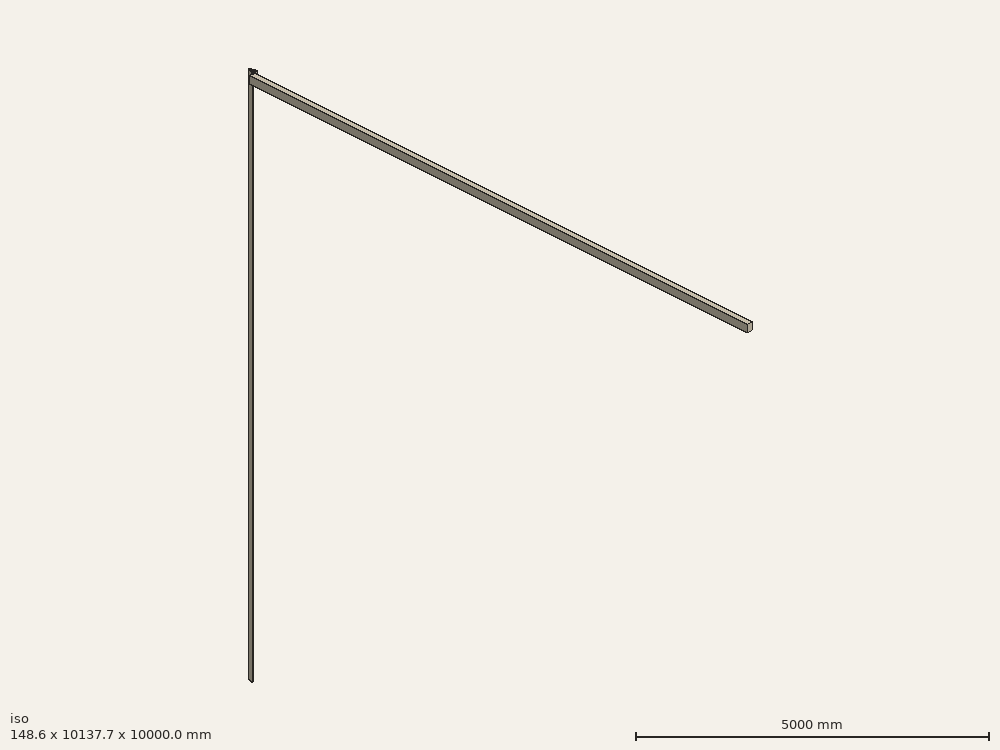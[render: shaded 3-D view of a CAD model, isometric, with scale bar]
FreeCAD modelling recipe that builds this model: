
FCSTD DOCUMENT  (FreeCAD 0.16R)
Label: iPadHolder
License: All rights reserved
LicenseURL: http://en.wikipedia.org/wiki/All_rights_reserved
objects: Sketcher::SketchObject×4, PartDesign::Chamfer×4, PartDesign::Pocket×3, PartDesign::Pad×1, Mesh::Feature×1
note: 16 computed .brp shape members not serialized (recipe doc carries the construction recipe); baked Part::Feature solids carry a one-line shape summary decoded from their .brp

FEATURE [Sketcher::SketchObject] Sketch
  sketch-geometry (27):
    g0: LineSegment StartX=-10 StartY=136.068 StartZ=0 EndX=-10 EndY=6.60009 EndZ=0
    g1: LineSegment StartX=-16.6001 StartY=0 StartZ=0 EndX=-78.7772 EndY=0 EndZ=0
    g2: LineSegment StartX=-80 StartY=-1.22284 StartZ=0 EndX=-80 EndY=-12.8107 EndZ=0
    g3: LineSegment StartX=-77.8107 StartY=-15 StartZ=0 EndX=25.8977 EndY=-15 EndZ=0
    g4: LineSegment StartX=28.76 StartY=-11.3687 StartZ=0 EndX=-6.74605 EndY=136.453 EndZ=0
    g5: LineSegment StartX=8.19725 StartY=15.8213 StartZ=0 EndX=15.8617 EndY=8.1568 EndZ=0
    g6: LineSegment StartX=15.8617 StartY=2.27255 StartZ=0 EndX=9.06464 EndY=-4.52454 EndZ=0
    g7: LineSegment StartX=7.32986 StartY=-4.52454 StartZ=0 EndX=-0.53498 EndY=3.3403 EndZ=0
    g8: LineSegment StartX=-0.53498 StartY=7.08905 StartZ=0 EndX=8.19725 EndY=15.8213 EndZ=0
    g9: LineSegment StartX=-2.82086 StartY=88.5548 StartZ=0 EndX=-4.52651 EndY=31.7136 EndZ=0
    g10: LineSegment StartX=-1.22545 StartY=28.2083 StartZ=0 EndX=8.07744 EndY=27.9291 EndZ=0
    g11: LineSegment StartX=11.5203 StartY=31.9185 StartZ=0 EndX=2.8702 EndY=80.3321 EndZ=0
    g12: LineSegment StartX=2.8702 StartY=80.3321 StartZ=0 EndX=-2.82086 EndY=88.5548 EndZ=0
    g13: ArcOfCircle CenterX=-8.35021 CenterY=136.068 CenterZ=0 NormalX=0 NormalY=0 NormalZ=1 Radius=1.64979 StartAngle=0.23573 EndAngle=3.14159
    g14: ArcOfCircle CenterX=-16.6001 CenterY=6.60009 CenterZ=0 NormalX=0 NormalY=0 NormalZ=1 Radius=6.60009 StartAngle=4.71239 EndAngle=6.28319
    g15: ArcOfCircle CenterX=25.8977 CenterY=-12.0562 CenterZ=0 NormalX=0 NormalY=0 NormalZ=1 Radius=2.94379 StartAngle=4.71239 EndAngle=6.51892
    g16: ArcOfCircle CenterX=-77.8107 CenterY=-12.8107 CenterZ=0 NormalX=0 NormalY=0 NormalZ=1 Radius=2.18926 StartAngle=3.14159 EndAngle=4.71239
    g17: ArcOfCircle CenterX=-78.7772 CenterY=-1.22284 CenterZ=0 NormalX=0 NormalY=0 NormalZ=1 Radius=1.22284 StartAngle=1.5708 EndAngle=3.14159
    g18: ArcOfCircle CenterX=1.33939 CenterY=5.21467 CenterZ=0 NormalX=0 NormalY=0 NormalZ=1 Radius=2.65076 StartAngle=2.35619 EndAngle=3.92699
    g19: ArcOfCircle CenterX=8.19725 CenterY=-3.65715 CenterZ=0 NormalX=0 NormalY=0 NormalZ=1 Radius=1.22668 StartAngle=3.92699 EndAngle=5.49779
    g20: ArcOfCircle CenterX=12.9196 CenterY=5.21467 CenterZ=0 NormalX=0 NormalY=0 NormalZ=1 Radius=4.1608 StartAngle=5.49779 EndAngle=7.06858
    g21: ArcOfCircle CenterX=-1.12333 CenterY=31.6114 CenterZ=0 NormalX=0 NormalY=0 NormalZ=1 Radius=3.40471 StartAngle=3.11159 EndAngle=4.68239
    g22: ArcOfCircle CenterX=8.17924 CenterY=31.3216 CenterZ=0 NormalX=0 NormalY=0 NormalZ=1 Radius=3.394 StartAngle=4.68239 EndAngle=6.45999
    g23: LineSegment [constr] StartX=-40.8694 StartY=-9.0364 StartZ=0 EndX=-13.954 EndY=143.609 EndZ=0
    g24: LineSegment [constr] StartX=-13.954 StartY=143.609 StartZ=0 EndX=-21.8324 EndY=144.998 EndZ=0
    g25: LineSegment [constr] StartX=-21.8324 StartY=144.998 StartZ=0 EndX=-48.7479 EndY=-7.64721 EndZ=0
    g26: LineSegment [constr] StartX=-48.7479 StartY=-7.64721 StartZ=0 EndX=-40.8694 EndY=-9.0364 EndZ=0
  constraints (40):
    c: Vertical(g0)
    c: Vertical(g2)
    c: Horizontal(g3)
    c: Coincident(g8,g5)
    c: Angle(g7,g8) = 1.5708
    c: Angle(g5) = -0.785398
    c: Coincident(g11,g12)
    c: Coincident(g12,g9)
    c: Perpendicular(g9,g10)
    c: Distance(g12) = 10
    c: Tangent(g0,g13) = -1.5708
    c: Tangent(g4,g13) = -1.5708
    c: Tangent(g1,g14) = 1.5708
    c: Tangent(g0,g14) = 1.5708
    c: Tangent(g3,g15) = -1.5708
    c: Tangent(g4,g15) = -1.5708
    c: Tangent(g3,g16) = -1.5708
    c: Tangent(g2,g16) = -1.5708
    c: Tangent(g2,g17) = -1.5708
    c: Tangent(g1,g17) = -1.5708
    c: Tangent(g7,g18) = 1.5708
    c: Tangent(g8,g18) = 1.5708
    c: Tangent(g7,g19) = 1.5708
    c: Tangent(g6,g19) = 1.5708
    c: Tangent(g5,g20) = 1.5708
    c: Tangent(g6,g20) = 1.5708
    c: Tangent(g10,g21) = -1.5708
    c: Tangent(g9,g21) = -1.5708
    c: Tangent(g11,g22) = -1.5708
    c: Tangent(g10,g22) = -1.5708
    c: Coincident(g23,g24)
    c: Coincident(g24,g25)
    c: Coincident(g25,g26)
    c: Coincident(g26,g23)
    c: Distance(g24) = 8
    c: Perpendicular(g24,g25)
    c: Parallel(g23,g25)
    c: Distance(g23) = 155
    c: Perpendicular(g23,g26)
    c: Angle(g23) = 1.39626
FEATURE [PartDesign::Pad] Pad
  Length = 180
  Length2 = 100
  Sketch = -> Sketch
  Type = 0
FEATURE [Sketcher::SketchObject] Sketch001
  Placement = pos=(0,0,180) rot=(0,0,1;0rad)
  Support = -> Pad [Face25]
  sketch-geometry (4):
    g0: LineSegment StartX=-24.6725 StartY=127.645 StartZ=0 EndX=-65.954 EndY=-4.51379 EndZ=0
    g1: LineSegment StartX=-65.954 StartY=-4.51379 StartZ=0 EndX=-58.4086 EndY=-7.1721 EndZ=0
    g2: LineSegment StartX=-58.4086 StartY=-7.1721 StartZ=0 EndX=-16.7735 EndY=126.119 EndZ=0
    g3: LineSegment StartX=-16.7735 StartY=126.119 StartZ=0 EndX=-24.6725 EndY=127.645 EndZ=0
  constraints (6):
    c: Coincident(g0,g1)
    c: Coincident(g1,g2)
    c: Coincident(g2,g3)
    c: Coincident(g3,g0)
    c: Distance(g1) = 8
    c: Parallel(g2,g0)
FEATURE [PartDesign::Pocket] Pocket
  Length = 5
  Sketch = -> Sketch001
  Type = 1
FEATURE [Sketcher::SketchObject] Sketch003
  ExternalGeometry = -> [Pocket]
  Placement = pos=(0,0,0) rot=(0,0.707107,0.707107;3.14159rad)
  Support = -> Pocket [Face1]
  sketch-geometry (4):
    g0: LineSegment StartX=119.737 StartY=160 StartZ=0 EndX=19.737 EndY=160 EndZ=0
    g1: LineSegment StartX=19.737 StartY=160 StartZ=0 EndX=19.737 EndY=20 EndZ=0
    g2: LineSegment StartX=19.737 StartY=20 StartZ=0 EndX=119.737 EndY=20 EndZ=0
    g3: LineSegment StartX=119.737 StartY=20 StartZ=0 EndX=119.737 EndY=160 EndZ=0
  constraints (12):
    c: Coincident(g0,g1)
    c: Coincident(g1,g2)
    c: Coincident(g2,g3)
    c: Coincident(g3,g0)
    c: Horizontal(g0)
    c: Horizontal(g2)
    c: Vertical(g1)
    c: Vertical(g3)
    c: Distance(g0) = 100
    c: Distance(g3) = 140
    c: Distance(g1,g-5) = 20
    c: DistanceX(g2) = 119.737
FEATURE [PartDesign::Pocket] Pocket001
  Length = 5
  Sketch = -> Sketch003
  Type = 1
FEATURE [Sketcher::SketchObject] Sketch004
  ExternalGeometry = -> [Pocket001]
  Placement = pos=(-10,0,0) rot=(0.57735,-0.57735,-0.57735;2.0944rad)
  Support = -> Pocket001 [Face10]
  sketch-geometry (10):
    g0: LineSegment StartX=-6.60009 StartY=160 StartZ=0 EndX=-90 EndY=160 EndZ=0
    g1: LineSegment StartX=-90 StartY=160 StartZ=0 EndX=-120 EndY=130 EndZ=0
    g2: LineSegment StartX=-120 StartY=130 StartZ=0 EndX=-90 EndY=100 EndZ=0
    g3: LineSegment StartX=-90 StartY=100 StartZ=0 EndX=-6.60009 EndY=100 EndZ=0
    g4: LineSegment StartX=-6.60009 StartY=100 StartZ=0 EndX=-6.60009 EndY=160 EndZ=0
    g5: LineSegment StartX=-90 StartY=80 StartZ=0 EndX=-120 EndY=50 EndZ=0
    g6: LineSegment StartX=-120 StartY=50 StartZ=0 EndX=-90 EndY=20 EndZ=0
    g7: LineSegment StartX=-90 StartY=20 StartZ=0 EndX=-6.60009 EndY=20 EndZ=0
    g8: LineSegment StartX=-6.60009 StartY=20 StartZ=0 EndX=-6.60009 EndY=80 EndZ=0
    g9: LineSegment StartX=-6.60009 StartY=80 StartZ=0 EndX=-90 EndY=80 EndZ=0
  constraints (30):
    c: Horizontal(g0)
    c: Coincident(g0,g1)
    c: Coincident(g1,g2)
    c: Coincident(g2,g3)
    c: Horizontal(g3)
    c: Coincident(g3,g4)
    c: Coincident(g4,g0)
    c: Coincident(g5,g6)
    c: Coincident(g6,g7)
    c: Coincident(g7,g8)
    c: Coincident(g8,g9)
    c: Coincident(g9,g5)
    c: Horizontal(g9)
    c: Horizontal(g7)
    c: Vertical(g8)
    c: Vertical(g4)
    c: Angle(g6,g5) = 1.5708
    c: Angle(g2,g1) = 1.5708
    c: Angle(g2) = -0.785398
    c: Angle(g6) = -0.785398
    c: PointOnObject(g8,g-3)
    c: PointOnObject(g3,g-3)
    c: Distance(g0,g-3) = 20
    c: Distance(g-3,g7) = 20
    c: Distance(g8,g3) = 20
    c: DistanceY(g8) = 80
    c: DistanceX(g5) = -120
    c: DistanceX(g1) = -120
    c: Equal(g2,g1)
    c: Equal(g6,g5)
FEATURE [PartDesign::Pocket] Pocket002
  Length = 5
  Sketch = -> Sketch004
  Type = 1
FEATURE [PartDesign::Chamfer] Chamfer
  Base = -> Pocket002 [Edge57,Edge58,Edge59,Edge60,Edge61,Edge62,Edge63,Edge64,Edge65,Edge66,Edge67,Edge68,Edge55,Edge7,Edge69,Edge70,Edge71,Edge72,Edge73,Edge74,Edge75,Edge76,Edge77,Edge78,Edge79,Edge80,Edge81]
  Size = 1
FEATURE [PartDesign::Chamfer] Chamfer001
  Base = -> Chamfer [Edge24,Edge32,Edge33,Edge34,Edge35,Edge36,Edge37,Edge38,Edge39,Edge40,Edge41,Edge42,Edge43,Edge6,Edge44,Edge45,Edge46,Edge47,Edge48,Edge49,Edge50,Edge51,Edge52,Edge53,Edge54,Edge55,Edge56]
  Size = 1
FEATURE [PartDesign::Chamfer] Chamfer002
  Base = -> Chamfer001 [Edge6,Edge23,Edge28,Edge29,Edge30,Edge31,Edge32,Edge33,Edge34,Edge35,Edge36,Edge37,Edge38,Edge26,Edge7,Edge39,Edge40,Edge41,Edge42,Edge43,Edge8,Edge44]
  Size = 1
FEATURE [PartDesign::Chamfer] Chamfer003
  Base = -> Chamfer002 [Edge149,Edge320,Edge9,Edge1]
  Size = 1
FEATURE [Mesh::Feature] Mesh  label="Chamfer003 (Meshed)"
